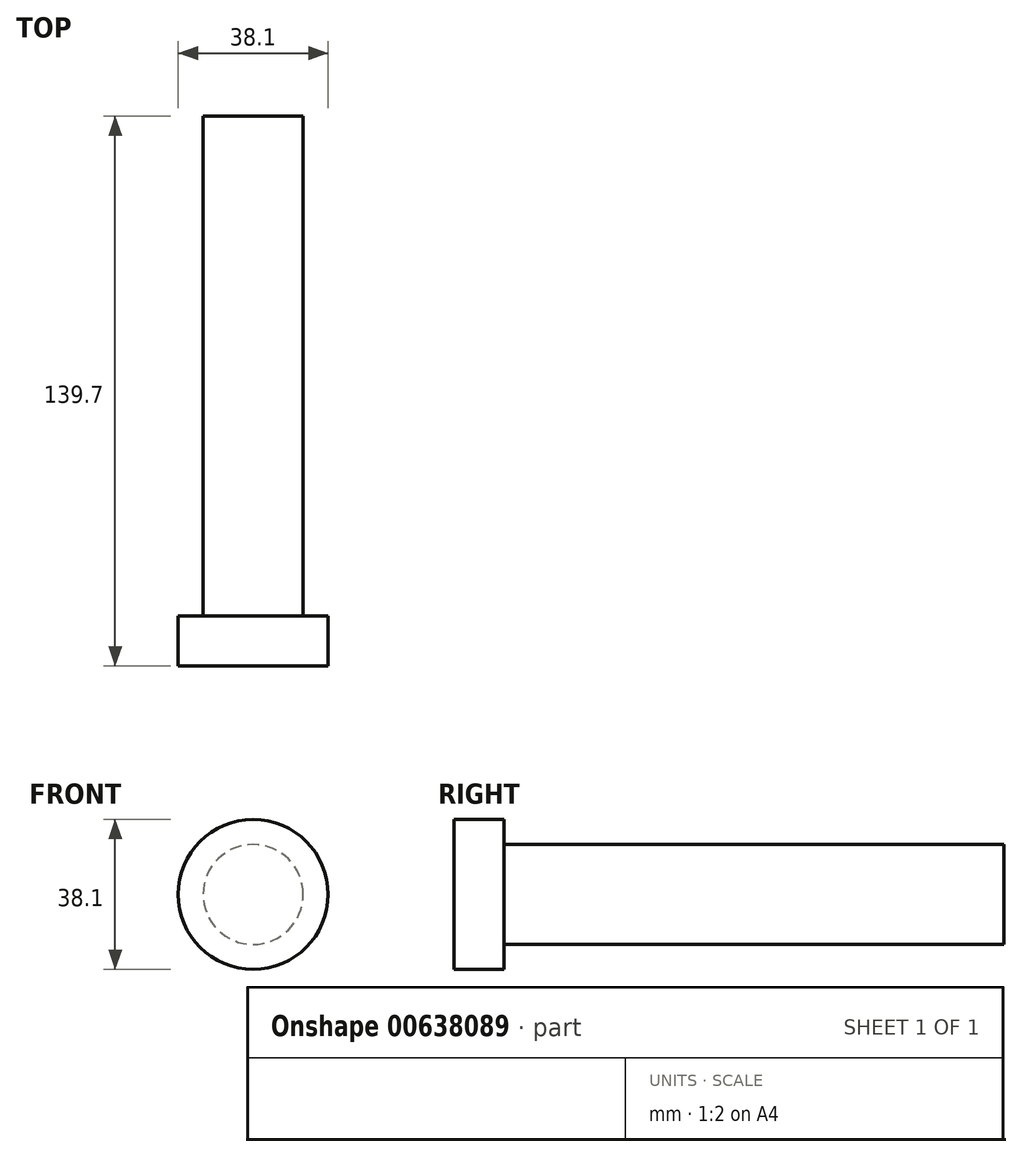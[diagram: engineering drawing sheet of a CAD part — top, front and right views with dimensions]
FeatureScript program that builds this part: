
annotation { "Feature Type Name" : "Feature", "Feature Type Description" : "" }
export const myFeature = defineFeature(function(context is Context, id is Id, definition is map)
    precondition{}
    {
        {
            var Q0;
            Q0=qCreatedBy(makeId("Front.planeOp"),FACE);
            var sketch = newSketch(context, id + "F0", { "sketchPlane" : qUnion([Q0])});
            skCircle(sketch, "E0", {"center": v(0, 0) * mm, "radius": 12.7 * mm});
            skSolve(sketch);
        }
        {
            var Q0;
            Q0=makeQuery(id+"F0.imprint","IMPRINT",FACE,{"disambiguationData":[TD([[makeQuery(id+"F0.imprint","IMPRINT",EDGE,{"derivedFrom":sQuery(id+"F0.wireOp",EDGE,"E0")}),1.0]])]});
            extrude(context, id + "F1", {"entities" : qUnion([Q0]), "depth" : 127 * mm, "offsetDistance" : 25.4 * mm});
        }
        {
            var Q0;
            Q0=makeQuery(id+"F1.opExtrude","CAP_FACE",FACE,{"disambiguationData":[OSD([sQuery(id+"F0.wireOp",EDGE,"E0")])],"isStart":false});
            var sketch = newSketch(context, id + "F2", { "sketchPlane" : qUnion([Q0])});
            skCircle(sketch, "E1", {"center": v(0, 0) * mm, "radius": 19.05 * mm});
            skSolve(sketch);
        }
        {
            var Q0;
            Q0=makeQuery(id+"F2.imprint","IMPRINT",FACE,{"disambiguationData":[TD([[makeQuery(id+"F2.imprint","IMPRINT",EDGE,{"derivedFrom":sQuery(id+"F2.wireOp",EDGE,"E1")}),1.0]])]});
            var Q1;
            Q1=makeQuery(id+"F2.imprint","IMPRINT",FACE,{"disambiguationData":[TD([[makeQuery(id+"F2.imprint","IMPRINT",EDGE,{"derivedFrom":makeQuery(id+"F1.opExtrude","CAP_EDGE",EDGE,{"disambiguationData":[OSD([sQuery(id+"F0.wireOp",EDGE,"E0")])],"isStart":false})}),1.0]])]});
            extrude(context, id + "F3", {"entities" : qUnion([Q0, Q1]), "operationType" : NewBodyOperationType.ADD, "depth" : 12.7 * mm, "offsetDistance" : 25.4 * mm});
        }
    });
